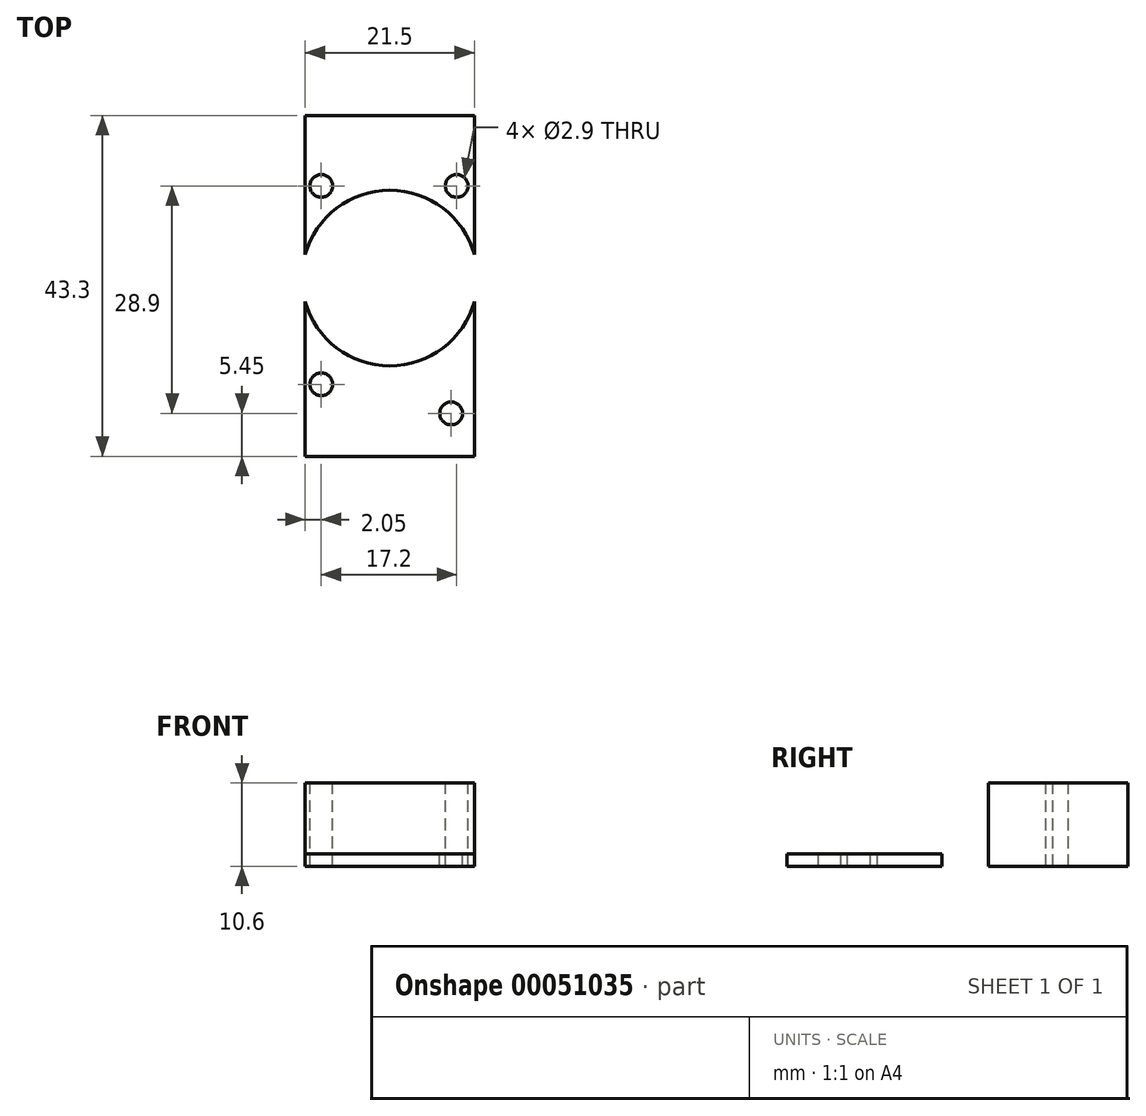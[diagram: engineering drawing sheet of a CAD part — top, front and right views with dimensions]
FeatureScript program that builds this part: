
annotation { "Feature Type Name" : "Feature", "Feature Type Description" : "" }
export const myFeature = defineFeature(function(context is Context, id is Id, definition is map)
    precondition{}
    {
        {
            var Q0;
            Q0=qCreatedBy(makeId("Top.planeOp"),FACE);
            var sketch = newSketch(context, id + "F0", { "sketchPlane" : qUnion([Q0])});
            skLineSegment(sketch, "E0.rect.bottom", {"start": v(-10.75, -21.65) * mm, "end": v(10.75, -21.65) * mm});
            skLineSegment(sketch, "E0.rect.top", {"start": v(-10.75, 21.65) * mm, "end": v(10.75, 21.65) * mm});
            skLineSegment(sketch, "E0.rect.left", {"start": v(-10.75, -21.65) * mm, "end": v(-10.75, 21.65) * mm});
            skLineSegment(sketch, "E0.rect.right", {"start": v(10.75, -21.65) * mm, "end": v(10.75, 21.65) * mm});
            skPoint(sketch, "E0.rect.middle", {"position": v(0, 0) * mm});
            skCircle(sketch, "E1", {"center": v(-8.7, 12.7) * mm, "radius": 1.45 * mm});
            skCircle(sketch, "E2", {"center": v(8.5, 12.7) * mm, "radius": 1.45 * mm});
            skCircle(sketch, "E3", {"center": v(-8.7, -12.5) * mm, "radius": 1.45 * mm});
            skCircle(sketch, "E4", {"center": v(7.8, -16.2) * mm, "radius": 1.45 * mm});
            skLineSegment(sketch, "E5", {"start": v(-10.75, 12.7) * mm, "end": v(10.75, 12.7) * mm, "construction": true});
            skLineSegment(sketch, "E6", {"start": v(-8.7, 21.65) * mm, "end": v(-8.7, -21.65) * mm, "construction": true});
            skCircle(sketch, "E7", {"center": v(0, 1) * mm, "radius": 11.15 * mm});
            skSolve(sketch);
        }
        {
            var Q0;
            {var subQ0=sQuery(id+"F0.wireOp",EDGE,"E0.rect.top");Q0=makeQuery(id+"F0.imprint","IMPRINT",FACE,{"disambiguationData":[TD([[makeQuery(id+"F0.imprint","IMPRINT",EDGE,{"derivedFrom":subQ0}),-1.0]])]});}
            var Q1;
            {var subQ0=sQuery(id+"F0.wireOp",EDGE,"E7");var subQ1=sQuery(id+"F0.wireOp",EDGE,"E0.rect.left");var subQ2=makeQuery(id+"F0.imprint","INTERSECT",VERTEX,{"disambiguationData":[OD(0.0)],"derivedFrom":[subQ1,subQ0]});Q1=makeQuery(id+"F0.imprint","IMPRINT",FACE,{"disambiguationData":[TD([[makeQuery(id+"F0.imprint","IMPRINT",EDGE,{"disambiguationData":[TD([[subQ2,-1.0]])],"derivedFrom":subQ1}),-1.0]])]});}
            var Q2;
            {var subQ1=sQuery(id+"F0.wireOp",EDGE,"E0.rect.bottom");Q2=makeQuery(id+"F0.imprint","IMPRINT",FACE,{"disambiguationData":[TD([[makeQuery(id+"F0.imprint","IMPRINT",EDGE,{"derivedFrom":subQ1}),1.0]])]});}
            extrude(context, id + "F1", {"entities" : qUnion([Q0, Q1, Q2]), "oppositeDirection" : true, "depth" : 1.6 * mm});
        }
        {
            var Q0;
            {var subQ0=sQuery(id+"F0.wireOp",EDGE,"E7");var subQ1=sQuery(id+"F0.wireOp",EDGE,"E0.rect.left");var subQ2=makeQuery(id+"F0.imprint","INTERSECT",VERTEX,{"disambiguationData":[OD(0.0)],"derivedFrom":[subQ1,subQ0]});Q0=makeQuery(id+"F0.imprint","IMPRINT",FACE,{"disambiguationData":[TD([[makeQuery(id+"F0.imprint","IMPRINT",EDGE,{"disambiguationData":[TD([[subQ2,-1.0]])],"derivedFrom":subQ1}),-1.0]])]});}
            var Q1;
            {var subQ0=sQuery(id+"F0.wireOp",EDGE,"E7");var subQ1=sQuery(id+"F0.wireOp",EDGE,"E0.rect.left");var subQ2=makeQuery(id+"F0.imprint","INTERSECT",VERTEX,{"disambiguationData":[OD(0.0)],"derivedFrom":[subQ1,subQ0]});Q1=makeQuery(id+"F0.imprint","IMPRINT",FACE,{"disambiguationData":[TD([[makeQuery(id+"F0.imprint","IMPRINT",EDGE,{"disambiguationData":[TD([[subQ2,-1.0]])],"derivedFrom":subQ1}),1.0]])]});}
            var Q2;
            {var subQ0=sQuery(id+"F0.wireOp",EDGE,"E7");var subQ1=sQuery(id+"F0.wireOp",EDGE,"E0.rect.right");var subQ2=makeQuery(id+"F0.imprint","INTERSECT",VERTEX,{"disambiguationData":[OD(0.0)],"derivedFrom":[subQ1,subQ0]});Q2=makeQuery(id+"F0.imprint","IMPRINT",FACE,{"disambiguationData":[TD([[makeQuery(id+"F0.imprint","IMPRINT",EDGE,{"disambiguationData":[TD([[subQ2,-1.0]])],"derivedFrom":subQ1}),-1.0]])]});}
            extrude(context, id + "F2", {"entities" : qUnion([Q0, Q1, Q2]), "operationType" : NewBodyOperationType.ADD, "depth" : 9 * mm});
        }
        {
            var Q0;
            Q0=makeQuery(id+"F1.opExtrude","CAP_FACE",FACE,{"disambiguationData":[OSD([sQuery(id+"F0.wireOp",EDGE,"E0.rect.bottom"),sQuery(id+"F0.wireOp",EDGE,"E0.rect.top"),sQuery(id+"F0.wireOp",EDGE,"E0.rect.left"),sQuery(id+"F0.wireOp",EDGE,"E0.rect.right"),sQuery(id+"F0.wireOp",EDGE,"E1"),sQuery(id+"F0.wireOp",EDGE,"E2"),sQuery(id+"F0.wireOp",EDGE,"E3"),sQuery(id+"F0.wireOp",EDGE,"E4")])],"isStart":false});
            var sketch = newSketch(context, id + "F3", { "sketchPlane" : qUnion([Q0])});
            skLineSegment(sketch, "E8.0.0", {"start": v(-10.75, -21.65) * mm, "end": v(10.75, -21.65) * mm});
            skLineSegment(sketch, "E8.0.1", {"start": v(10.75, -21.65) * mm, "end": v(10.75, 21.65) * mm});
            skLineSegment(sketch, "E8.0.2", {"start": v(10.75, 21.65) * mm, "end": v(-10.75, 21.65) * mm});
            skLineSegment(sketch, "E8.0.3", {"start": v(-10.75, 21.65) * mm, "end": v(-10.75, -21.65) * mm});
            skLineSegment(sketch, "E9.bottom", {"start": v(7.62, -21.45) * mm, "end": v(-7.62, -21.45) * mm});
            skLineSegment(sketch, "E9.top", {"start": v(7.62, -18.95) * mm, "end": v(-7.62, -18.95) * mm});
            skLineSegment(sketch, "E9.left", {"start": v(7.62, -21.45) * mm, "end": v(7.62, -18.95) * mm});
            skLineSegment(sketch, "E9.right", {"start": v(-7.62, -21.45) * mm, "end": v(-7.62, -18.95) * mm});
            skLineSegment(sketch, "E10", {"start": v(0, -21.65) * mm, "end": v(0, -13.3) * mm, "construction": true});
            skPoint(sketch, "E10.endSnap0", {"position": v(0, -21.65) * mm});
            skLineSegment(sketch, "E11", {"start": v(5.08, -21.45) * mm, "end": v(5.08, -18.95) * mm});
            skSolve(sketch);
        }
    });
